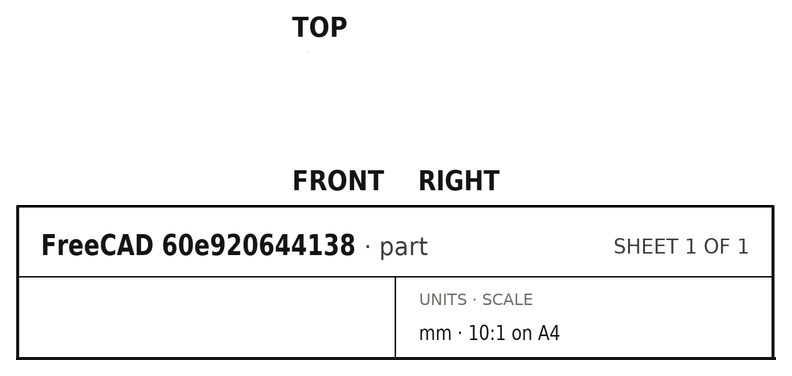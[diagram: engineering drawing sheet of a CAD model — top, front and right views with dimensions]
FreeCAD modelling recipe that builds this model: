
FCSTD DOCUMENT  (FreeCAD 0.21R33694 (Git))
Label: coax
License: All rights reserved
LicenseURL: http://en.wikipedia.org/wiki/All_rights_reserved
objects: Part::Part2DObjectPython×6, Part::Cut×3, App::FeaturePython×3
note: 9 computed .brp shape members not serialized (recipe doc carries the construction recipe); baked Part::Feature solids carry a one-line shape summary decoded from their .brp

FEATURE [Part::Part2DObjectPython] Polygon  # Draft 2D object (typed FeaturePython)
  Area = 5.17315e-07
  ChamferSize = 0
  DrawMode = 0
  FacesNumber = 80
  FilletRadius = 0
  MakeFace = true
  Radius = 0.000406
FEATURE [Part::Part2DObjectPython] Polygon001  # Draft 2D object (typed FeaturePython)
  Area = 6.87427e-06
  ChamferSize = 0
  DrawMode = 0
  FacesNumber = 80
  FilletRadius = 0
  MakeFace = true
  Radius = 0.00148
FEATURE [Part::Part2DObjectPython] Rectangle  # Draft 2D object (typed FeaturePython)
  Area = 1.5e-05
  ChamferSize = 0
  Columns = 1
  FilletRadius = 0
  Height = 0.003
  Length = 0.005
  MakeFace = true
  Placement = pos=(-0.0025,-0.003,0) rot=(0,0,1;0rad)
  Rows = 1
FEATURE [Part::Cut] Cut
  Base = -> Polygon001
  Tool = -> Polygon
FEATURE [Part::Part2DObjectPython] Rectangle001  # Draft 2D object (typed FeaturePython)
  Area = 1.5e-05
  ChamferSize = 0
  Columns = 1
  FilletRadius = 0
  Height = 0.003
  Length = 0.005
  MakeFace = true
  Placement = pos=(-0.000353553,0.00388909,0) rot=(0,0,1;3.92699rad)
  Rows = 1
FEATURE [Part::Cut] Cut001
  Base = -> Cut
  Tool = -> Rectangle
FEATURE [Part::Cut] Cut002
  Base = -> Cut001
  Tool = -> Rectangle001
FEATURE [Part::Part2DObjectPython] Line  label="_Pv"  # Draft 2D object (typed FeaturePython)
  Area = 0
  ChamferSize = 0
  Closed = false
  End = (0.00148,0,0)
  FilletRadius = 0
  Length = 0.001074
  MakeFace = true
  Placement = pos=(0.000406,0,0) rot=(0,0,1;0rad)
  Points = (2) [(0,0,0),(0.001074,-6.57635e-20,0)]
  Start = (0.000406,0,0)
  Subdivisions = 0
FEATURE [App::FeaturePython] Text  label="_M1(voltage){v}"  # WARN: FeaturePython — macro-defined, semantics opaque (R4)
  Placement = pos=(-0.000829707,-0.00286884,0) rot=(0,0,1;0rad)
  Text = .
FEATURE [App::FeaturePython] Text001  label="_Bpmc1(PMC){v}"  # WARN: FeaturePython — macro-defined, semantics opaque (R4)
  Placement = pos=(-0.000829707,-0.00286884,0) rot=(0,0,1;0rad)
  Text = .
FEATURE [App::FeaturePython] Text002  label="_Bpmc2(PMC){pmc}"  # WARN: FeaturePython — macro-defined, semantics opaque (R4)
  Placement = pos=(-0.000829707,-0.00286884,0) rot=(0,0,1;0rad)
  Text = .
FEATURE [Part::Part2DObjectPython] Line001  label="_Ppmc"  # Draft 2D object (typed FeaturePython)
  Area = 0
  ChamferSize = 0
  Closed = false
  End = (0.00104652,0.00104652,0)
  FilletRadius = 0
  Length = 0.001074
  MakeFace = true
  Placement = pos=(0.000287085,0.000287085,0) rot=(0.864922,0.231754,0.445197;1.08358rad)
  Points = (2) [(0,0,0),(0.0010374,0.000159438,-0.000227702)]
  Start = (0.000287085,0.000287085,0)
  Subdivisions = 0
